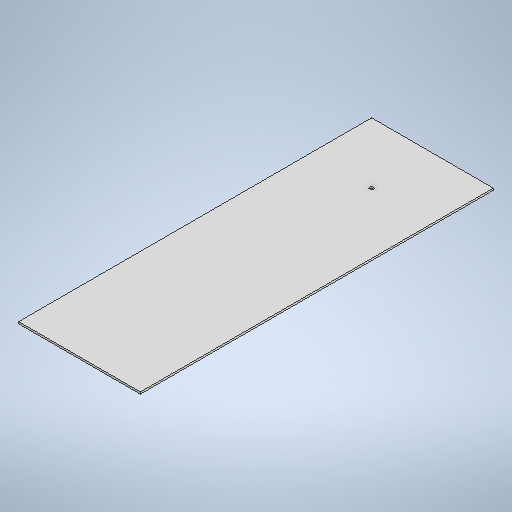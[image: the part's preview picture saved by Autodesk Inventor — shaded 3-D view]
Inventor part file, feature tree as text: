
AUTODESK INVENTOR PART (.ipt)
format: ipt  version: 2025.2 (Build 292293000, 293)  size: 229,888 bytes
history: native  units: mm
features: extrude x2, sketch x2
ambient origin geometry x8: Origin, YZ Plane, XZ Plane, XY Plane, X Axis, Y Axis, Z Axis, Center Point
bodies: Solid1 (feature_tree)
feature tree (4):
  extrude  "Extrusion1"  Depth=200.0mm
  extrude  "Extrusion2"  Depth=3.175mm
  sketch  "Sketch1"  dims[d0=200.0mm d1=480.0mm]
  sketch  "Sketch2"  dims[d2=3.175mm d3=0.0mm d5=6.35mm d6=3.175mm d7=0.0mm]
